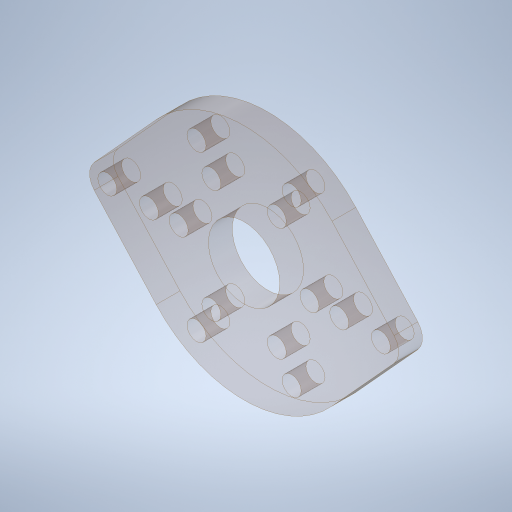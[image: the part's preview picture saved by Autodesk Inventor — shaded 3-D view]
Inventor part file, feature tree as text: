
AUTODESK INVENTOR PART (.ipt)
format: ipt  version: 2023.4 (Build 274418000, 418)  size: 327,168 bytes
history: native  units: in
note: dims shown in document units (in); Inventor stores cm internally (conversion verified against a paired STEP export)
features: sketch x1, extrude x1, hole x1
ambient origin geometry x8: Origin, YZ Plane, XZ Plane, XY Plane, X Axis, Y Axis, Z Axis, Center Point
bodies: Solid1 (feature_tree)
feature tree (3):
  sketch  "Sketch1"  dims[d0=0.75in d1=2.5in d2=0.375in d3=1.375in d8=0.25in d9=0.0in d18=2.0in d19=2.3622in d21=360.0deg d23=0.201in d24=0.75in d25=0.385in d26=0.25in d27=0.5635in d28=1.0in d29=0.8108in]
  extrude  "Extrusion1"  Depth=2.5in
  hole  "Hole2"  [1 undecoded]
note: 1 required parameter value undecoded (feature->parameter linkage not recoverable at this tier; creation-order binding heuristic only, values carry confidence <= 0.55)
